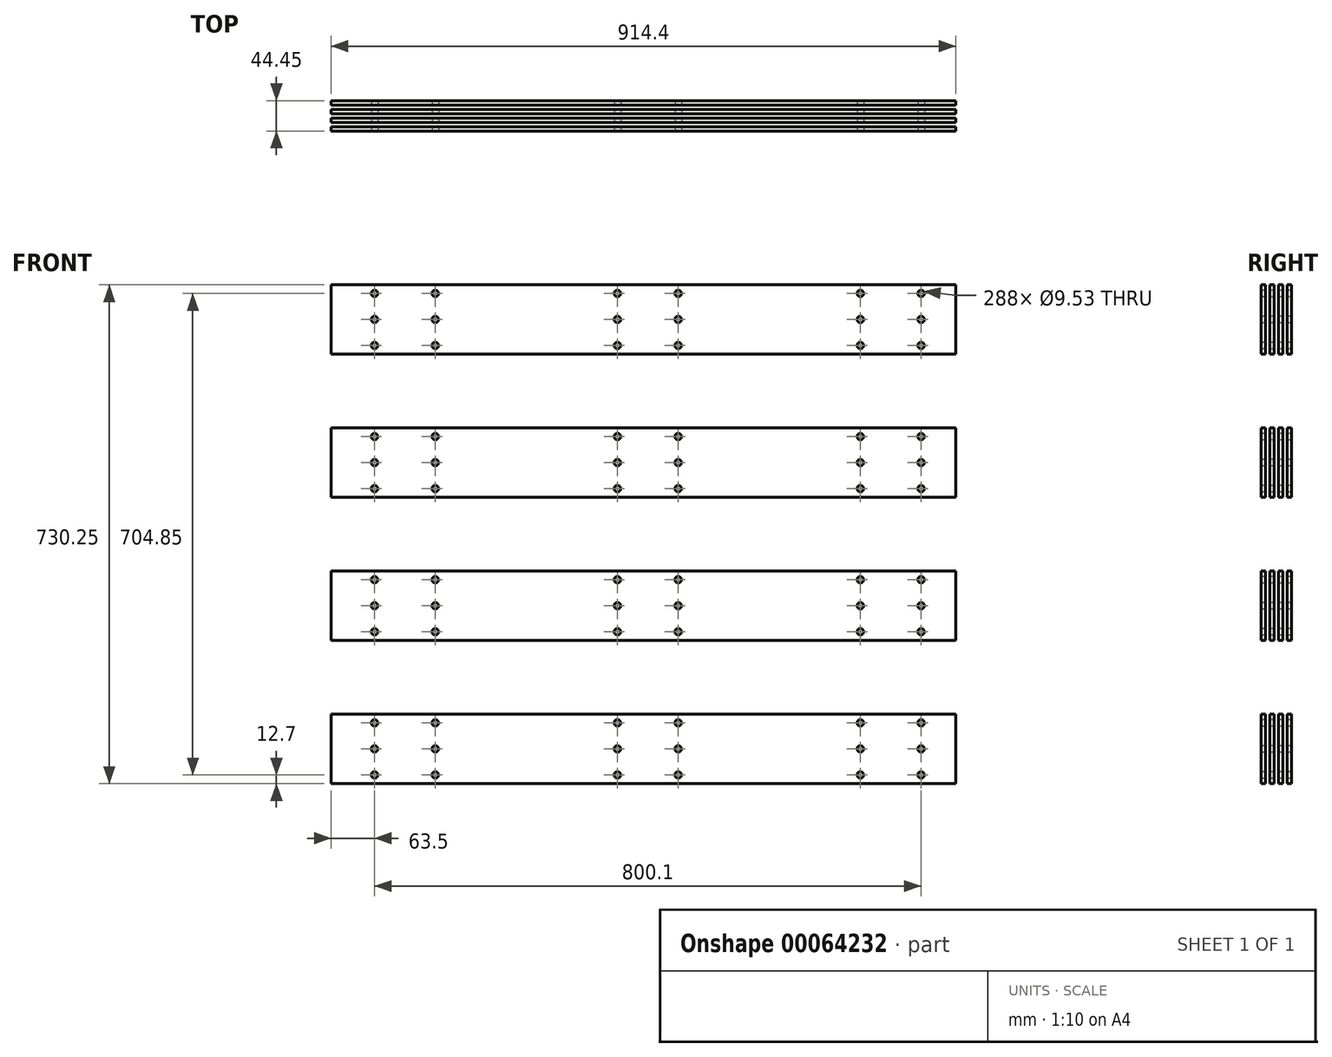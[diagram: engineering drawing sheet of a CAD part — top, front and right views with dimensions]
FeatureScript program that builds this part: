
annotation { "Feature Type Name" : "Feature", "Feature Type Description" : "" }
export const myFeature = defineFeature(function(context is Context, id is Id, definition is map)
    precondition{}
    {
        {
            var Q0;
            Q0=qCreatedBy(makeId("Right.planeOp"),FACE);
            var sketch = newSketch(context, id + "F0", { "sketchPlane" : qUnion([Q0])});
            skLineSegment(sketch, "E0.bottom", {"start": v(0, 0) * mm, "end": v(6.35, 0) * mm});
            skLineSegment(sketch, "E0.top", {"start": v(0, 101.6) * mm, "end": v(6.35, 101.6) * mm});
            skLineSegment(sketch, "E0.left", {"start": v(0, 0) * mm, "end": v(0, 101.6) * mm});
            skLineSegment(sketch, "E0.right", {"start": v(6.35, 0) * mm, "end": v(6.35, 101.6) * mm});
            skLineSegment(sketch, "E1.0.1.0", {"start": v(0, -209.55) * mm, "end": v(0, -107.95) * mm});
            skLineSegment(sketch, "E1.0.1.1", {"start": v(6.35, -209.55) * mm, "end": v(6.35, -107.95) * mm});
            skLineSegment(sketch, "E1.0.1.2", {"start": v(0, -107.95) * mm, "end": v(6.35, -107.95) * mm});
            skLineSegment(sketch, "E1.0.1.3", {"start": v(0, -209.55) * mm, "end": v(6.35, -209.55) * mm});
            skLineSegment(sketch, "E1.0.2.0", {"start": v(0, -419.1) * mm, "end": v(0, -317.5) * mm});
            skLineSegment(sketch, "E1.0.2.1", {"start": v(6.35, -419.1) * mm, "end": v(6.35, -317.5) * mm});
            skLineSegment(sketch, "E1.0.2.2", {"start": v(0, -317.5) * mm, "end": v(6.35, -317.5) * mm});
            skLineSegment(sketch, "E1.0.2.3", {"start": v(0, -419.1) * mm, "end": v(6.35, -419.1) * mm});
            skLineSegment(sketch, "E1.0.3.0", {"start": v(0, -628.65) * mm, "end": v(0, -527.05) * mm});
            skLineSegment(sketch, "E1.0.3.1", {"start": v(6.35, -628.65) * mm, "end": v(6.35, -527.05) * mm});
            skLineSegment(sketch, "E1.0.3.2", {"start": v(0, -527.05) * mm, "end": v(6.35, -527.05) * mm});
            skLineSegment(sketch, "E1.0.3.3", {"start": v(0, -628.65) * mm, "end": v(6.35, -628.65) * mm});
            skLineSegment(sketch, "E1.1.0.0", {"start": v(12.7, 0) * mm, "end": v(12.7, 101.6) * mm});
            skLineSegment(sketch, "E1.1.0.1", {"start": v(19.05, 0) * mm, "end": v(19.05, 101.6) * mm});
            skLineSegment(sketch, "E1.1.0.2", {"start": v(12.7, 101.6) * mm, "end": v(19.05, 101.6) * mm});
            skLineSegment(sketch, "E1.1.0.3", {"start": v(12.7, 0) * mm, "end": v(19.05, 0) * mm});
            skLineSegment(sketch, "E1.1.1.0", {"start": v(12.7, -209.55) * mm, "end": v(12.7, -107.95) * mm});
            skLineSegment(sketch, "E1.1.1.1", {"start": v(19.05, -209.55) * mm, "end": v(19.05, -107.95) * mm});
            skLineSegment(sketch, "E1.1.1.2", {"start": v(12.7, -107.95) * mm, "end": v(19.05, -107.95) * mm});
            skLineSegment(sketch, "E1.1.1.3", {"start": v(12.7, -209.55) * mm, "end": v(19.05, -209.55) * mm});
            skLineSegment(sketch, "E1.1.2.0", {"start": v(12.7, -419.1) * mm, "end": v(12.7, -317.5) * mm});
            skLineSegment(sketch, "E1.1.2.1", {"start": v(19.05, -419.1) * mm, "end": v(19.05, -317.5) * mm});
            skLineSegment(sketch, "E1.1.2.2", {"start": v(12.7, -317.5) * mm, "end": v(19.05, -317.5) * mm});
            skLineSegment(sketch, "E1.1.2.3", {"start": v(12.7, -419.1) * mm, "end": v(19.05, -419.1) * mm});
            skLineSegment(sketch, "E1.1.3.0", {"start": v(12.7, -628.65) * mm, "end": v(12.7, -527.05) * mm});
            skLineSegment(sketch, "E1.1.3.1", {"start": v(19.05, -628.65) * mm, "end": v(19.05, -527.05) * mm});
            skLineSegment(sketch, "E1.1.3.2", {"start": v(12.7, -527.05) * mm, "end": v(19.05, -527.05) * mm});
            skLineSegment(sketch, "E1.1.3.3", {"start": v(12.7, -628.65) * mm, "end": v(19.05, -628.65) * mm});
            skLineSegment(sketch, "E1.2.0.0", {"start": v(25.4, 0) * mm, "end": v(25.4, 101.6) * mm});
            skLineSegment(sketch, "E1.2.0.1", {"start": v(31.75, 0) * mm, "end": v(31.75, 101.6) * mm});
            skLineSegment(sketch, "E1.2.0.2", {"start": v(25.4, 101.6) * mm, "end": v(31.75, 101.6) * mm});
            skLineSegment(sketch, "E1.2.0.3", {"start": v(25.4, 0) * mm, "end": v(31.75, 0) * mm});
            skLineSegment(sketch, "E1.2.1.0", {"start": v(25.4, -209.55) * mm, "end": v(25.4, -107.95) * mm});
            skLineSegment(sketch, "E1.2.1.1", {"start": v(31.75, -209.55) * mm, "end": v(31.75, -107.95) * mm});
            skLineSegment(sketch, "E1.2.1.2", {"start": v(25.4, -107.95) * mm, "end": v(31.75, -107.95) * mm});
            skLineSegment(sketch, "E1.2.1.3", {"start": v(25.4, -209.55) * mm, "end": v(31.75, -209.55) * mm});
            skLineSegment(sketch, "E1.2.2.0", {"start": v(25.4, -419.1) * mm, "end": v(25.4, -317.5) * mm});
            skLineSegment(sketch, "E1.2.2.1", {"start": v(31.75, -419.1) * mm, "end": v(31.75, -317.5) * mm});
            skLineSegment(sketch, "E1.2.2.2", {"start": v(25.4, -317.5) * mm, "end": v(31.75, -317.5) * mm});
            skLineSegment(sketch, "E1.2.2.3", {"start": v(25.4, -419.1) * mm, "end": v(31.75, -419.1) * mm});
            skLineSegment(sketch, "E1.2.3.0", {"start": v(25.4, -628.65) * mm, "end": v(25.4, -527.05) * mm});
            skLineSegment(sketch, "E1.2.3.1", {"start": v(31.75, -628.65) * mm, "end": v(31.75, -527.05) * mm});
            skLineSegment(sketch, "E1.2.3.2", {"start": v(25.4, -527.05) * mm, "end": v(31.75, -527.05) * mm});
            skLineSegment(sketch, "E1.2.3.3", {"start": v(25.4, -628.65) * mm, "end": v(31.75, -628.65) * mm});
            skLineSegment(sketch, "E1.3.0.0", {"start": v(38.1, 0) * mm, "end": v(38.1, 101.6) * mm});
            skLineSegment(sketch, "E1.3.0.1", {"start": v(44.45, 0) * mm, "end": v(44.45, 101.6) * mm});
            skLineSegment(sketch, "E1.3.0.2", {"start": v(38.1, 101.6) * mm, "end": v(44.45, 101.6) * mm});
            skLineSegment(sketch, "E1.3.0.3", {"start": v(38.1, 0) * mm, "end": v(44.45, 0) * mm});
            skLineSegment(sketch, "E1.3.1.0", {"start": v(38.1, -209.55) * mm, "end": v(38.1, -107.95) * mm});
            skLineSegment(sketch, "E1.3.1.1", {"start": v(44.45, -209.55) * mm, "end": v(44.45, -107.95) * mm});
            skLineSegment(sketch, "E1.3.1.2", {"start": v(38.1, -107.95) * mm, "end": v(44.45, -107.95) * mm});
            skLineSegment(sketch, "E1.3.1.3", {"start": v(38.1, -209.55) * mm, "end": v(44.45, -209.55) * mm});
            skLineSegment(sketch, "E1.3.2.0", {"start": v(38.1, -419.1) * mm, "end": v(38.1, -317.5) * mm});
            skLineSegment(sketch, "E1.3.2.1", {"start": v(44.45, -419.1) * mm, "end": v(44.45, -317.5) * mm});
            skLineSegment(sketch, "E1.3.2.2", {"start": v(38.1, -317.5) * mm, "end": v(44.45, -317.5) * mm});
            skLineSegment(sketch, "E1.3.2.3", {"start": v(38.1, -419.1) * mm, "end": v(44.45, -419.1) * mm});
            skLineSegment(sketch, "E1.3.3.0", {"start": v(38.1, -628.65) * mm, "end": v(38.1, -527.05) * mm});
            skLineSegment(sketch, "E1.3.3.1", {"start": v(44.45, -628.65) * mm, "end": v(44.45, -527.05) * mm});
            skLineSegment(sketch, "E1.3.3.2", {"start": v(38.1, -527.05) * mm, "end": v(44.45, -527.05) * mm});
            skLineSegment(sketch, "E1.3.3.3", {"start": v(38.1, -628.65) * mm, "end": v(44.45, -628.65) * mm});
            skLineSegment(sketch, "E1.direction1", {"start": v(0, 0) * mm, "end": v(12.7, 0) * mm, "construction": true});
            skLineSegment(sketch, "E1.direction2", {"start": v(0, 0) * mm, "end": v(0, -209.55) * mm, "construction": true});
            skSolve(sketch);
        }
        {
            var Q0;
            Q0=qSketchRegion(id+"F0",true);
            extrude(context, id + "F1", {"entities" : qUnion([Q0]), "endBound" : BoundingType.SYMMETRIC, "depth" : 914.4 * mm});
        }
        {
            var Q0;
            Q0=makeQuery(id+"F1.opExtrude","SWEPT_FACE",FACE,{"disambiguationData":[OSD([sQuery(id+"F0.wireOp",EDGE,"E0.left")])]});
            var sketch = newSketch(context, id + "F2", { "sketchPlane" : qUnion([Q0])});
            skCircle(sketch, "E2", {"center": v(406.4, 88.9) * mm, "radius": 4.76 * mm});
            skCircle(sketch, "E3.0.1.0", {"center": v(406.4, 50.8) * mm, "radius": 4.76 * mm});
            skCircle(sketch, "E3.0.2.0", {"center": v(406.4, 12.7) * mm, "radius": 4.76 * mm});
            skCircle(sketch, "E3.1.0.0", {"center": v(317.5, 88.9) * mm, "radius": 4.76 * mm});
            skCircle(sketch, "E3.1.1.0", {"center": v(317.5, 50.8) * mm, "radius": 4.76 * mm});
            skCircle(sketch, "E3.1.2.0", {"center": v(317.5, 12.7) * mm, "radius": 4.76 * mm});
            skLineSegment(sketch, "E3.direction1", {"start": v(406.4, 88.9) * mm, "end": v(317.5, 88.9) * mm, "construction": true});
            skLineSegment(sketch, "E3.direction2", {"start": v(406.4, 88.9) * mm, "end": v(406.4, 50.8) * mm, "construction": true});
            skLineSegment(sketch, "E4.0.1.0", {"start": v(406.4, -120.65) * mm, "end": v(406.4, -158.75) * mm, "construction": true});
            skLineSegment(sketch, "E4.0.1.1", {"start": v(406.4, -120.65) * mm, "end": v(317.5, -120.65) * mm, "construction": true});
            skCircle(sketch, "E4.0.1.2", {"center": v(317.5, -158.75) * mm, "radius": 4.76 * mm});
            skCircle(sketch, "E4.0.1.3", {"center": v(406.4, -158.75) * mm, "radius": 4.76 * mm});
            skCircle(sketch, "E4.0.1.4", {"center": v(317.5, -120.65) * mm, "radius": 4.76 * mm});
            skCircle(sketch, "E4.0.1.5", {"center": v(406.4, -120.65) * mm, "radius": 4.76 * mm});
            skCircle(sketch, "E4.0.1.6", {"center": v(406.4, -196.85) * mm, "radius": 4.76 * mm});
            skCircle(sketch, "E4.0.1.7", {"center": v(317.5, -196.85) * mm, "radius": 4.76 * mm});
            skLineSegment(sketch, "E4.0.2.0", {"start": v(406.4, -330.2) * mm, "end": v(406.4, -368.3) * mm, "construction": true});
            skLineSegment(sketch, "E4.0.2.1", {"start": v(406.4, -330.2) * mm, "end": v(317.5, -330.2) * mm, "construction": true});
            skCircle(sketch, "E4.0.2.2", {"center": v(317.5, -368.3) * mm, "radius": 4.76 * mm});
            skCircle(sketch, "E4.0.2.3", {"center": v(406.4, -368.3) * mm, "radius": 4.76 * mm});
            skCircle(sketch, "E4.0.2.4", {"center": v(317.5, -330.2) * mm, "radius": 4.76 * mm});
            skCircle(sketch, "E4.0.2.5", {"center": v(406.4, -330.2) * mm, "radius": 4.76 * mm});
            skCircle(sketch, "E4.0.2.6", {"center": v(406.4, -406.4) * mm, "radius": 4.76 * mm});
            skCircle(sketch, "E4.0.2.7", {"center": v(317.5, -406.4) * mm, "radius": 4.76 * mm});
            skLineSegment(sketch, "E4.0.3.0", {"start": v(406.4, -539.75) * mm, "end": v(406.4, -577.85) * mm, "construction": true});
            skLineSegment(sketch, "E4.0.3.1", {"start": v(406.4, -539.75) * mm, "end": v(317.5, -539.75) * mm, "construction": true});
            skCircle(sketch, "E4.0.3.2", {"center": v(317.5, -577.85) * mm, "radius": 4.76 * mm});
            skCircle(sketch, "E4.0.3.3", {"center": v(406.4, -577.85) * mm, "radius": 4.76 * mm});
            skCircle(sketch, "E4.0.3.4", {"center": v(317.5, -539.75) * mm, "radius": 4.76 * mm});
            skCircle(sketch, "E4.0.3.5", {"center": v(406.4, -539.75) * mm, "radius": 4.76 * mm});
            skCircle(sketch, "E4.0.3.6", {"center": v(406.4, -615.95) * mm, "radius": 4.76 * mm});
            skCircle(sketch, "E4.0.3.7", {"center": v(317.5, -615.95) * mm, "radius": 4.76 * mm});
            skLineSegment(sketch, "E4.1.0.0", {"start": v(50.8, 88.9) * mm, "end": v(50.8, 50.8) * mm, "construction": true});
            skLineSegment(sketch, "E4.1.0.1", {"start": v(50.8, 88.9) * mm, "end": v(-38.1, 88.9) * mm, "construction": true});
            skCircle(sketch, "E4.1.0.2", {"center": v(-38.1, 50.8) * mm, "radius": 4.76 * mm});
            skCircle(sketch, "E4.1.0.3", {"center": v(50.8, 50.8) * mm, "radius": 4.76 * mm});
            skCircle(sketch, "E4.1.0.4", {"center": v(-38.1, 88.9) * mm, "radius": 4.76 * mm});
            skCircle(sketch, "E4.1.0.5", {"center": v(50.8, 88.9) * mm, "radius": 4.76 * mm});
            skCircle(sketch, "E4.1.0.6", {"center": v(50.8, 12.7) * mm, "radius": 4.76 * mm});
            skCircle(sketch, "E4.1.0.7", {"center": v(-38.1, 12.7) * mm, "radius": 4.76 * mm});
            skLineSegment(sketch, "E4.1.1.0", {"start": v(50.8, -120.65) * mm, "end": v(50.8, -158.75) * mm, "construction": true});
            skLineSegment(sketch, "E4.1.1.1", {"start": v(50.8, -120.65) * mm, "end": v(-38.1, -120.65) * mm, "construction": true});
            skCircle(sketch, "E4.1.1.2", {"center": v(-38.1, -158.75) * mm, "radius": 4.76 * mm});
            skCircle(sketch, "E4.1.1.3", {"center": v(50.8, -158.75) * mm, "radius": 4.76 * mm});
            skCircle(sketch, "E4.1.1.4", {"center": v(-38.1, -120.65) * mm, "radius": 4.76 * mm});
            skCircle(sketch, "E4.1.1.5", {"center": v(50.8, -120.65) * mm, "radius": 4.76 * mm});
            skCircle(sketch, "E4.1.1.6", {"center": v(50.8, -196.85) * mm, "radius": 4.76 * mm});
            skCircle(sketch, "E4.1.1.7", {"center": v(-38.1, -196.85) * mm, "radius": 4.76 * mm});
            skLineSegment(sketch, "E4.1.2.0", {"start": v(50.8, -330.2) * mm, "end": v(50.8, -368.3) * mm, "construction": true});
            skLineSegment(sketch, "E4.1.2.1", {"start": v(50.8, -330.2) * mm, "end": v(-38.1, -330.2) * mm, "construction": true});
            skCircle(sketch, "E4.1.2.2", {"center": v(-38.1, -368.3) * mm, "radius": 4.76 * mm});
            skCircle(sketch, "E4.1.2.3", {"center": v(50.8, -368.3) * mm, "radius": 4.76 * mm});
            skCircle(sketch, "E4.1.2.4", {"center": v(-38.1, -330.2) * mm, "radius": 4.76 * mm});
            skCircle(sketch, "E4.1.2.5", {"center": v(50.8, -330.2) * mm, "radius": 4.76 * mm});
            skCircle(sketch, "E4.1.2.6", {"center": v(50.8, -406.4) * mm, "radius": 4.76 * mm});
            skCircle(sketch, "E4.1.2.7", {"center": v(-38.1, -406.4) * mm, "radius": 4.76 * mm});
            skLineSegment(sketch, "E4.1.3.0", {"start": v(50.8, -539.75) * mm, "end": v(50.8, -577.85) * mm, "construction": true});
            skLineSegment(sketch, "E4.1.3.1", {"start": v(50.8, -539.75) * mm, "end": v(-38.1, -539.75) * mm, "construction": true});
            skCircle(sketch, "E4.1.3.2", {"center": v(-38.1, -577.85) * mm, "radius": 4.76 * mm});
            skCircle(sketch, "E4.1.3.3", {"center": v(50.8, -577.85) * mm, "radius": 4.76 * mm});
            skCircle(sketch, "E4.1.3.4", {"center": v(-38.1, -539.75) * mm, "radius": 4.76 * mm});
            skCircle(sketch, "E4.1.3.5", {"center": v(50.8, -539.75) * mm, "radius": 4.76 * mm});
            skCircle(sketch, "E4.1.3.6", {"center": v(50.8, -615.95) * mm, "radius": 4.76 * mm});
            skCircle(sketch, "E4.1.3.7", {"center": v(-38.1, -615.95) * mm, "radius": 4.76 * mm});
            skLineSegment(sketch, "E4.2.0.0", {"start": v(-304.8, 88.9) * mm, "end": v(-304.8, 50.8) * mm, "construction": true});
            skLineSegment(sketch, "E4.2.0.1", {"start": v(-304.8, 88.9) * mm, "end": v(-393.7, 88.9) * mm, "construction": true});
            skCircle(sketch, "E4.2.0.2", {"center": v(-393.7, 50.8) * mm, "radius": 4.76 * mm});
            skCircle(sketch, "E4.2.0.3", {"center": v(-304.8, 50.8) * mm, "radius": 4.76 * mm});
            skCircle(sketch, "E4.2.0.4", {"center": v(-393.7, 88.9) * mm, "radius": 4.76 * mm});
            skCircle(sketch, "E4.2.0.5", {"center": v(-304.8, 88.9) * mm, "radius": 4.76 * mm});
            skCircle(sketch, "E4.2.0.6", {"center": v(-304.8, 12.7) * mm, "radius": 4.76 * mm});
            skCircle(sketch, "E4.2.0.7", {"center": v(-393.7, 12.7) * mm, "radius": 4.76 * mm});
            skLineSegment(sketch, "E4.2.1.0", {"start": v(-304.8, -120.65) * mm, "end": v(-304.8, -158.75) * mm, "construction": true});
            skLineSegment(sketch, "E4.2.1.1", {"start": v(-304.8, -120.65) * mm, "end": v(-393.7, -120.65) * mm, "construction": true});
            skCircle(sketch, "E4.2.1.2", {"center": v(-393.7, -158.75) * mm, "radius": 4.76 * mm});
            skCircle(sketch, "E4.2.1.3", {"center": v(-304.8, -158.75) * mm, "radius": 4.76 * mm});
            skCircle(sketch, "E4.2.1.4", {"center": v(-393.7, -120.65) * mm, "radius": 4.76 * mm});
            skCircle(sketch, "E4.2.1.5", {"center": v(-304.8, -120.65) * mm, "radius": 4.76 * mm});
            skCircle(sketch, "E4.2.1.6", {"center": v(-304.8, -196.85) * mm, "radius": 4.76 * mm});
            skCircle(sketch, "E4.2.1.7", {"center": v(-393.7, -196.85) * mm, "radius": 4.76 * mm});
            skLineSegment(sketch, "E4.2.2.0", {"start": v(-304.8, -330.2) * mm, "end": v(-304.8, -368.3) * mm, "construction": true});
            skLineSegment(sketch, "E4.2.2.1", {"start": v(-304.8, -330.2) * mm, "end": v(-393.7, -330.2) * mm, "construction": true});
            skCircle(sketch, "E4.2.2.2", {"center": v(-393.7, -368.3) * mm, "radius": 4.76 * mm});
            skCircle(sketch, "E4.2.2.3", {"center": v(-304.8, -368.3) * mm, "radius": 4.76 * mm});
            skCircle(sketch, "E4.2.2.4", {"center": v(-393.7, -330.2) * mm, "radius": 4.76 * mm});
            skCircle(sketch, "E4.2.2.5", {"center": v(-304.8, -330.2) * mm, "radius": 4.76 * mm});
            skCircle(sketch, "E4.2.2.6", {"center": v(-304.8, -406.4) * mm, "radius": 4.76 * mm});
            skCircle(sketch, "E4.2.2.7", {"center": v(-393.7, -406.4) * mm, "radius": 4.76 * mm});
            skLineSegment(sketch, "E4.2.3.0", {"start": v(-304.8, -539.75) * mm, "end": v(-304.8, -577.85) * mm, "construction": true});
            skLineSegment(sketch, "E4.2.3.1", {"start": v(-304.8, -539.75) * mm, "end": v(-393.7, -539.75) * mm, "construction": true});
            skCircle(sketch, "E4.2.3.2", {"center": v(-393.7, -577.85) * mm, "radius": 4.76 * mm});
            skCircle(sketch, "E4.2.3.3", {"center": v(-304.8, -577.85) * mm, "radius": 4.76 * mm});
            skCircle(sketch, "E4.2.3.4", {"center": v(-393.7, -539.75) * mm, "radius": 4.76 * mm});
            skCircle(sketch, "E4.2.3.5", {"center": v(-304.8, -539.75) * mm, "radius": 4.76 * mm});
            skCircle(sketch, "E4.2.3.6", {"center": v(-304.8, -615.95) * mm, "radius": 4.76 * mm});
            skCircle(sketch, "E4.2.3.7", {"center": v(-393.7, -615.95) * mm, "radius": 4.76 * mm});
            skLineSegment(sketch, "E4.direction1", {"start": v(419.1, 50.8) * mm, "end": v(63.5, 50.8) * mm, "construction": true});
            skLineSegment(sketch, "E4.direction2", {"start": v(419.1, 50.8) * mm, "end": v(419.1, -158.75) * mm, "construction": true});
            skSolve(sketch);
        }
        {
            var Q0;
            Q0 = qSketchRegion(id + "F2", true);
            extrude(context, id + "F3", {"entities" : qUnion([Q0]), "operationType" : NewBodyOperationType.REMOVE, "endBound" : BoundingType.THROUGH_ALL, "oppositeDirection" : true, "depth" : 25.4 * mm});
        }
    });
